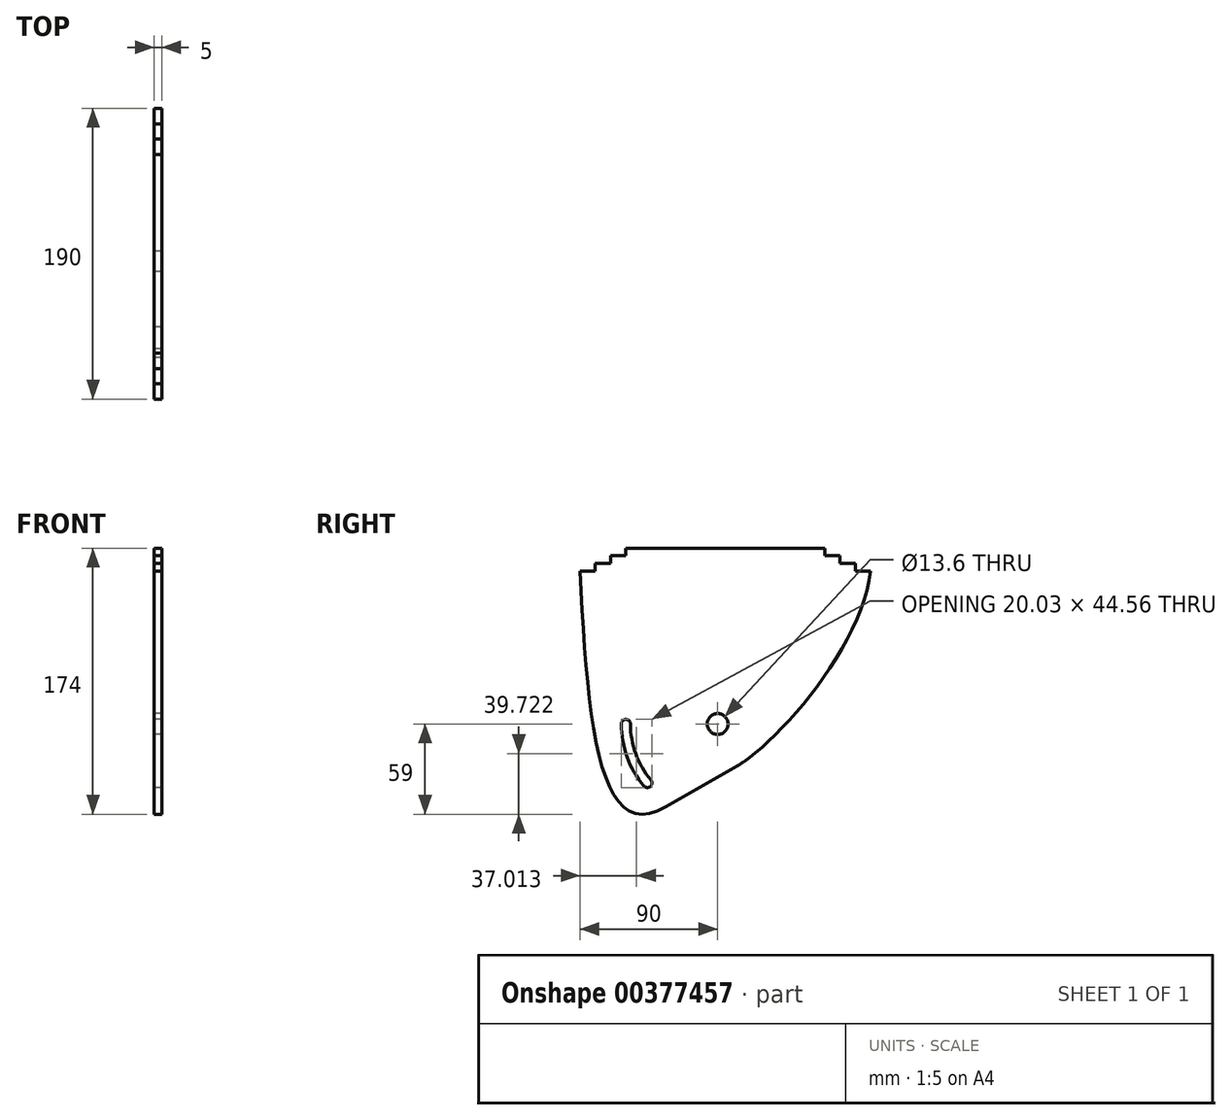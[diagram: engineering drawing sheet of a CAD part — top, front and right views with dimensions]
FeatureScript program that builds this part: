
annotation { "Feature Type Name" : "Feature", "Feature Type Description" : "" }
export const myFeature = defineFeature(function(context is Context, id is Id, definition is map)
    precondition{}
    {
        {
            var Q0;
            Q0=qCreatedBy(makeId("Right.planeOp"),FACE);
            var sketch = newSketch(context, id + "F0", { "sketchPlane" : qUnion([Q0])});
            skCircle(sketch, "E0", {"center": v(0, 0) * mm, "radius": 6.8 * mm});
            skArc(sketch, "E1", {"start": v(16.93, -24.77) * mm, "mid": v(15.97, -25.4) * mm, "end": v(15, -25.98) * mm});
            skLineSegment(sketch, "E2", {"start": v(15, -25.98) * mm, "end": v(-33.81, -54.16) * mm});
            skFitSpline(sketch, "E3", {"points": [v(-33.81, -54.16) * mm, v(-90, 100) * mm], "startDerivative": vector(-133.19, -76.9) * mm, "endDerivative": vector(-15.79, 300) * mm});
            skLineSegment(sketch, "E4", {"start": v(100, 100) * mm, "end": v(-90, 100) * mm});
            skFitSpline(sketch, "E5", {"points": [v(16.93, -24.77) * mm, v(100, 100) * mm], "startDerivative": vector(85.35, 58.32) * mm, "endDerivative": vector(16.39, 139.56) * mm});
            skSolve(sketch);
        }
        {
            var Q0;
            Q0=qCreatedBy(makeId("Right.planeOp"),FACE);
            var sketch = newSketch(context, id + "F1", { "sketchPlane" : qUnion([Q0])});
            skArc(sketch, "E6", {"start": v(-60, 0) * mm, "mid": v(-56.38, -20.52) * mm, "end": v(-45.96, -38.57) * mm, "construction": true});
            skArc(sketch, "E7.0.startCap", {"start": v(-63, 0) * mm, "mid": v(-60, 3) * mm, "end": v(-57, 0) * mm});
            skArc(sketch, "E7.0.endCap", {"start": v(-43.66, -36.64) * mm, "mid": v(-44.03, -40.87) * mm, "end": v(-48.26, -40.5) * mm});
            skArc(sketch, "E7.0.left", {"start": v(-57, 0) * mm, "mid": v(-53.56, -19.5) * mm, "end": v(-43.66, -36.64) * mm});
            skArc(sketch, "E7.0.right", {"start": v(-63, 0) * mm, "mid": v(-59.2, -21.55) * mm, "end": v(-48.26, -40.5) * mm});
            skLineSegment(sketch, "E8", {"start": v(0, 0) * mm, "end": v(-45.96, -38.57) * mm, "construction": true});
            skSolve(sketch);
        }
        {
            var Q0;
            Q0=qCreatedBy(makeId("Right.planeOp"),FACE);
            var sketch = newSketch(context, id + "F2", { "sketchPlane" : qUnion([Q0])});
            skLineSegment(sketch, "E9", {"start": v(-80, 100) * mm, "end": v(-80, 105) * mm});
            skLineSegment(sketch, "E10", {"start": v(-70, 105) * mm, "end": v(-80, 105) * mm});
            skLineSegment(sketch, "E11", {"start": v(-70, 105) * mm, "end": v(-70, 110) * mm});
            skLineSegment(sketch, "E12", {"start": v(5, 100) * mm, "end": v(5, 115.7) * mm, "construction": true});
            skLineSegment(sketch, "E13", {"start": v(-70, 110) * mm, "end": v(-60, 110) * mm});
            skLineSegment(sketch, "E14", {"start": v(-60, 110) * mm, "end": v(-60, 115) * mm});
            skLineSegment(sketch, "E15", {"start": v(-60, 115) * mm, "end": v(-50, 115) * mm});
            skLineSegment(sketch, "E16.MirrorCS", {"start": v(90, 100) * mm, "end": v(90, 105) * mm});
            skLineSegment(sketch, "E17.MirrorCS", {"start": v(80, 105) * mm, "end": v(90, 105) * mm});
            skLineSegment(sketch, "E18.MirrorCS", {"start": v(80, 105) * mm, "end": v(80, 110) * mm});
            skLineSegment(sketch, "E19.MirrorCS", {"start": v(80, 110) * mm, "end": v(70, 110) * mm});
            skLineSegment(sketch, "E20.MirrorCS", {"start": v(70, 115) * mm, "end": v(60, 115) * mm});
            skLineSegment(sketch, "E21.MirrorCS", {"start": v(70, 110) * mm, "end": v(70, 115) * mm});
            skLineSegment(sketch, "E22", {"start": v(-50, 115) * mm, "end": v(60, 115) * mm});
            skLineSegment(sketch, "E23", {"start": v(-80, 100) * mm, "end": v(90, 100) * mm});
            skSolve(sketch);
        }
        {
            var Q0;
            Q0 = qSketchRegion(id + "F0", true);
            extrude(context, id + "F3", {"entities" : qUnion([Q0]), "depth" : 5 * mm});
        }
        {
            var Q0;
            Q0 = qSketchRegion(id + "F1", true);
            extrude(context, id + "F4", {"entities" : qUnion([Q0]), "operationType" : NewBodyOperationType.REMOVE, "endBound" : BoundingType.THROUGH_ALL, "depth" : 25 * mm});
        }
        {
            var Q0;
            Q0 = qSketchRegion(id + "F2", true);
            extrude(context, id + "F5", {"entities" : qUnion([Q0]), "operationType" : NewBodyOperationType.ADD, "depth" : 5 * mm});
        }
    });
